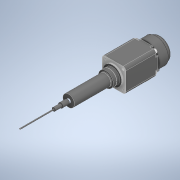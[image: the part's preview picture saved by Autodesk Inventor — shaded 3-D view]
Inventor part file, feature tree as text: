
AUTODESK INVENTOR PART (.ipt)
format: ipt  version: 2022 (Build 260153000, 153)  size: 339,456 bytes
history: native  units: in
note: dims shown in document units (in); Inventor stores cm internally (conversion verified against a paired STEP export)
features: extrude x3, sketch x3, other x2
ambient origin geometry x8: Origin, YZ Plane, XZ Plane, XY Plane, X Axis, Y Axis, Z Axis, Center Point
bodies: Solid2 (feature_tree), Solid3 (feature_tree), Solid4 (feature_tree), Solid1 (feature_tree)
feature tree (8):
  extrude  "Extrusion2"  Depth=0.2756in TaperAngle=0.0deg
  extrude  "Extrusion3"  Depth=1.2598in TaperAngle=0.0deg
  extrude  "Extrusion4"  Depth=1.6535in TaperAngle=0.0deg
  sketch  "Skizze2"  dims[d3=0.5043in d4=0.2756in d5=0.0in]
  sketch  "Skizze3"  dims[d6=0.3937in d7=1.2598in d8=0.0in]
  sketch  "Skizze4"  dims[d9=0.0394in d10=1.6535in d11=0.0in]
  other  "Solid2:1"
  other  "Solid3:1"
